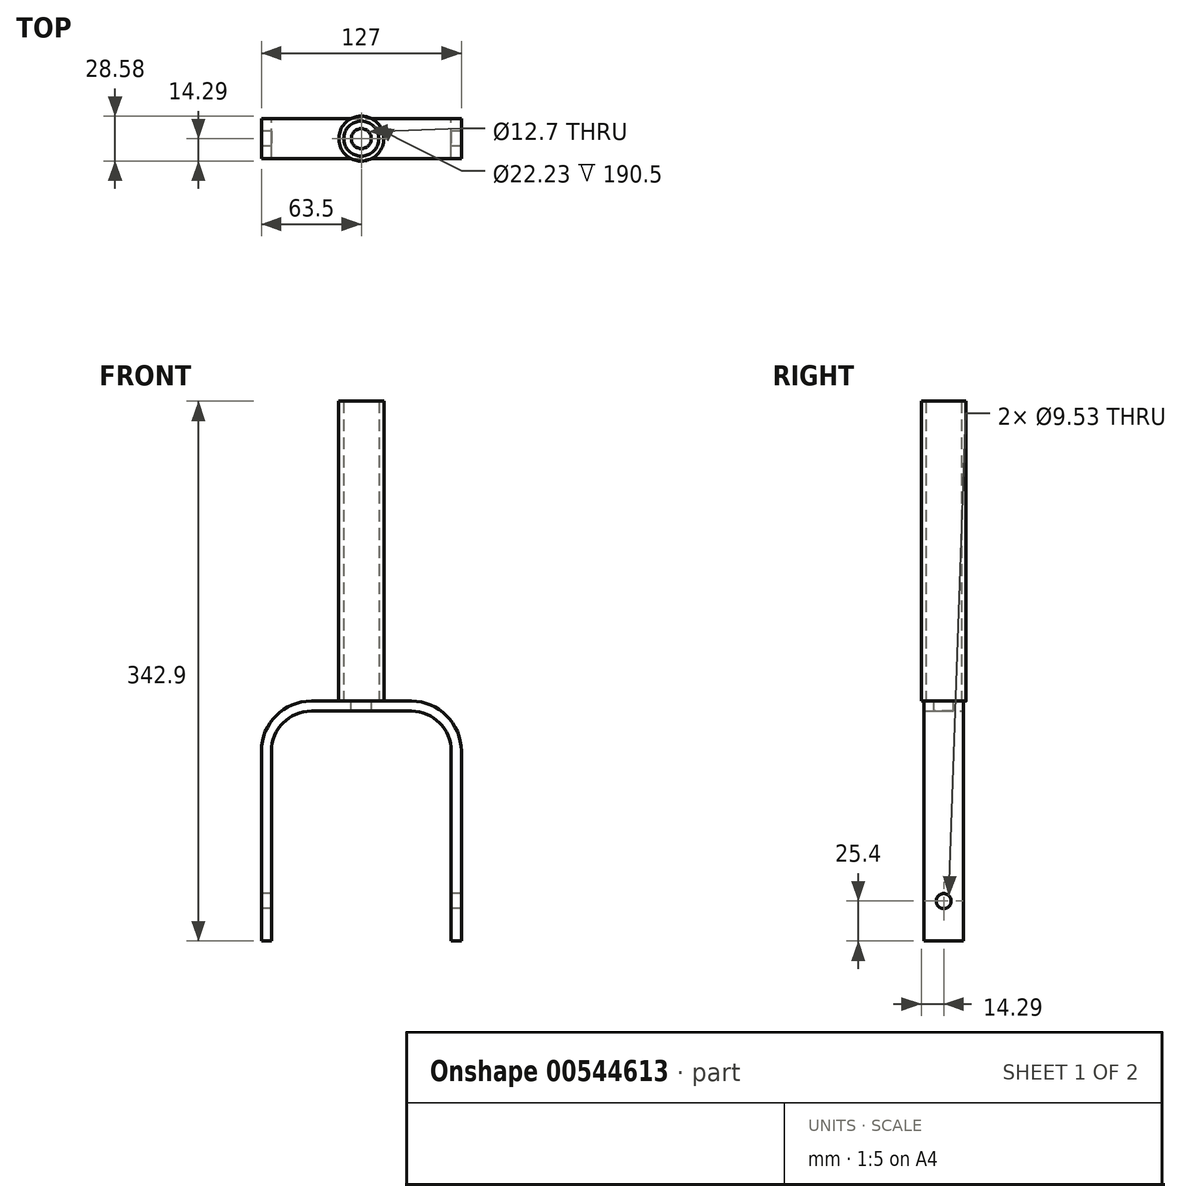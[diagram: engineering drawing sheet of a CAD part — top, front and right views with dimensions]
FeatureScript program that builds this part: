
annotation { "Feature Type Name" : "Feature", "Feature Type Description" : "" }
export const myFeature = defineFeature(function(context is Context, id is Id, definition is map)
    precondition{}
    {
        {
            var Q0;
            Q0=qCreatedBy(makeId("Front.planeOp"),FACE);
            var sketch = newSketch(context, id + "F0", { "sketchPlane" : qUnion([Q0])});
            skLineSegment(sketch, "E0", {"start": v(0, 0) * mm, "end": v(0, 152.4) * mm});
            skLineSegment(sketch, "E1.0", {"start": v(6.35, 0) * mm, "end": v(6.35, 146.05) * mm});
            skLineSegment(sketch, "E2", {"start": v(0, 152.4) * mm, "end": v(127, 152.4) * mm});
            skLineSegment(sketch, "E3", {"start": v(6.35, 146.05) * mm, "end": v(120.65, 146.05) * mm});
            skLineSegment(sketch, "E4", {"start": v(120.65, 146.05) * mm, "end": v(120.65, 0) * mm});
            skLineSegment(sketch, "E5", {"start": v(127, 152.4) * mm, "end": v(127, 0) * mm});
            skLineSegment(sketch, "E6", {"start": v(6.35, 0) * mm, "end": v(0, 0) * mm});
            skLineSegment(sketch, "E7", {"start": v(120.65, 0) * mm, "end": v(127, 0) * mm});
            skSolve(sketch);
        }
        {
            var Q0;
            Q0=makeQuery(id+"F0.imprint","IMPRINT",FACE,{"disambiguationData":[TD([[makeQuery(id+"F0.imprint","IMPRINT",EDGE,{"derivedFrom":sQuery(id+"F0.wireOp",EDGE,"E0")}),-1.0]])]});
            extrude(context, id + "F1", {"entities" : qUnion([Q0]), "endBound" : BoundingType.SYMMETRIC, "depth" : 25.4 * mm, "offsetDistance" : 25.4 * mm});
        }
        {
            var Q0;
            Q0=makeQuery(id+"F1.opExtrude","SWEPT_EDGE",EDGE,{"disambiguationData":[OSD([sQuery(id+"F0.wireOp",EDGE,"E1.0"),sQuery(id+"F0.wireOp",EDGE,"E3")])]});
            var Q1;
            Q1=makeQuery(id+"F1.opExtrude","SWEPT_EDGE",EDGE,{"disambiguationData":[OSD([sQuery(id+"F0.wireOp",EDGE,"E3"),sQuery(id+"F0.wireOp",EDGE,"E4")])]});
            fillet(context, id + "F2", {"entities" : qUnion([Q0, Q1]), "radius" : 25.4 * mm, "tangentPropagation" : true, "allowEdgeOverflow" : false});
        }
        {
            var Q0;
            Q0=makeQuery(id+"F1.opExtrude","SWEPT_EDGE",EDGE,{"disambiguationData":[OSD([sQuery(id+"F0.wireOp",EDGE,"E2"),sQuery(id+"F0.wireOp",EDGE,"E5")])]});
            var Q1;
            Q1=makeQuery(id+"F1.opExtrude","SWEPT_EDGE",EDGE,{"disambiguationData":[OSD([sQuery(id+"F0.wireOp",EDGE,"E0"),sQuery(id+"F0.wireOp",EDGE,"E2")])]});
            fillet(context, id + "F3", {"entities" : qUnion([Q0, Q1]), "radius" : 31.75 * mm, "tangentPropagation" : true, "allowEdgeOverflow" : false});
        }
        {
            var Q0;
            Q0=qCreatedBy(makeId("Right.planeOp"),FACE);
            var sketch = newSketch(context, id + "F4", { "sketchPlane" : qUnion([Q0])});
            skPoint(sketch, "E8", {"position": v(0, 25.4) * mm});
            skSolve(sketch);
        }
        {
            var Q0;
            Q0=sQuery(id+"F4.wireOp",VERTEX,"E8");
            var Q1;
            Q1=makeQuery(id+"F1.opExtrude","SWEPT_BODY",BODY,{"disambiguationData":[OSD([sQuery(id+"F0.wireOp",EDGE,"E0"),sQuery(id+"F0.wireOp",EDGE,"E1.0"),sQuery(id+"F0.wireOp",EDGE,"E2"),sQuery(id+"F0.wireOp",EDGE,"E3"),sQuery(id+"F0.wireOp",EDGE,"E4"),sQuery(id+"F0.wireOp",EDGE,"E5"),sQuery(id+"F0.wireOp",EDGE,"E6"),sQuery(id+"F0.wireOp",EDGE,"E7")])]});
            hole(context, id + "F5", {"style" : HoleStyle.SIMPLE, "endStyle" : HoleEndStyle.THROUGH, "oppositeDirection" : true, "holeDiameter" : 9.52 * mm, "majorDiameter" : 6.35 * mm, "isTappedThrough" : true, "tappedDepth" : 12.7 * mm, "tapClearance" : 3, "locations" : qUnion([Q0]), "scope" : qUnion([Q1])});
        }
        {
            var Q0;
            Q0=makeQuery(id+"F1.opExtrude","SWEPT_FACE",FACE,{"disambiguationData":[OSD([sQuery(id+"F0.wireOp",EDGE,"E2")])]});
            var sketch = newSketch(context, id + "F6", { "sketchPlane" : qUnion([Q0])});
            skPoint(sketch, "E9", {"position": v(63.5, 0) * mm});
            skLineSegment(sketch, "E10", {"start": v(95.25, 0) * mm, "end": v(31.75, 0) * mm, "construction": true});
            skSolve(sketch);
        }
        {
            var Q0;
            Q0=sQuery(id+"F6.wireOp",VERTEX,"E9");
            var Q1;
            Q1=makeQuery(id+"F1.opExtrude","SWEPT_BODY",BODY,{"disambiguationData":[OSD([sQuery(id+"F0.wireOp",EDGE,"E0"),sQuery(id+"F0.wireOp",EDGE,"E1.0"),sQuery(id+"F0.wireOp",EDGE,"E2"),sQuery(id+"F0.wireOp",EDGE,"E3"),sQuery(id+"F0.wireOp",EDGE,"E4"),sQuery(id+"F0.wireOp",EDGE,"E5"),sQuery(id+"F0.wireOp",EDGE,"E6"),sQuery(id+"F0.wireOp",EDGE,"E7")])]});
            hole(context, id + "F7", {"style" : HoleStyle.SIMPLE, "endStyle" : HoleEndStyle.THROUGH, "holeDiameter" : 12.7 * mm, "majorDiameter" : 6.35 * mm, "isTappedThrough" : true, "tappedDepth" : 12.7 * mm, "tapClearance" : 3, "locations" : qUnion([Q0]), "scope" : qUnion([Q1])});
        }
        {
            var Q0;
            Q0=makeQuery(id+"F1.opExtrude","SWEPT_FACE",FACE,{"disambiguationData":[OSD([sQuery(id+"F0.wireOp",EDGE,"E2")])]});
            var sketch = newSketch(context, id + "F8", { "sketchPlane" : qUnion([Q0])});
            skCircle(sketch, "E11", {"center": v(63.5, 0) * mm, "radius": 14.29 * mm});
            skCircle(sketch, "E12", {"center": v(63.5, 0) * mm, "radius": 11.11 * mm});
            skSolve(sketch);
        }
        {
            var Q0;
            Q0 = qSketchRegion(id + "F8", true);
            extrude(context, id + "F9", {"entities" : qUnion([Q0]), "operationType" : NewBodyOperationType.ADD, "depth" : 190.5 * mm, "offsetDistance" : 25.4 * mm});
        }
    });
